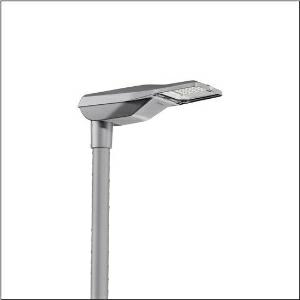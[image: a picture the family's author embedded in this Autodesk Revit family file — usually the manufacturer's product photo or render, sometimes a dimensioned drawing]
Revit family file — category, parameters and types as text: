
# Revit family: streetlight_sl_21_iq_micro___st1_5a_5xe1p31d08db_ec34
name_source: partatom
category: Lighting Fixtures
units: mm (PartAtom-declared; Revit-internal decimal feet)

## family parameters
Cut with Voids When Loaded = No
Host = Face
Light Source = No
Part Type = Normal
Room Calculation Point = No
Round Connector Dimension = Use Diameter
Shared = No

## types (1)
- --- (1 x LED, 4730 lm, 36.4 W, 3000K)
    Apparent Load = 36 VA
    CIE Flux Codes = 22 53 95 100 100
    Color Rendering = 70
    Color Temperature = 3000K
    Default Elevation = 1800 mm
    Description = Streetlight SL 21 iQ micro, mast luminaire, primary light control with lens, of PMMA, primary optical cover: cover, of toughened safety glass, transparent, light distribution: ST1.5a, light emission: direct distribution, primary light characteristic: asymmetric, installation type: post-top, side-entry, LED, High Power LED, rated luminous flux: 4.730lm, luminous efficacy: 130lm/W, light colour: 730, colour temperature: 3000K, control gear: iQ-Comfort, control: Auto-Match, Temp-Guard, Lumen-Switch, Night-Set, Smart-Wire, Light-Fading, Desk-Remote (wireless, voltage-free reading and setting of iQ features in the workshop via application-optimized NFC function/RFID function), optimised constant luminous flux control (CLO 2.0), pre-setting: linear dimming characteristic, mains connection: 220..240V, AC, 50/60Hz, start of lifetime: 36W, end of service life: 38W, reduction: 16W, luminaire housing, of diecast aluminium, powder-coated, Siteco® metallic grey (DB 702S), corrosivity category C5 mid according to DIN EN ISO 12944, please order mast flange separately, inclination adjustable: 0°, 5°, 10°, 15°, sealing non-destructively replaceable, multi-level sealing system, length: 528mm, width: 235mm, height: 110mm, mast flange for spigot size: 42mm (side-entry): 5XC10008XM4, 60/48mm (side-entry/post-top): 5XC10108XM2, 76/60mm (side-entry/post-top): 5XC10108XM1, protection rating (complete): IP66, insulation class (complete): insulation class II (safety insulation), certification: CE, ENEC, ENEC+, VDE, impact resistance: IK10, permissible operating ambient temperature for outdoor applications: -40..+50°C, standard-compliant lighting for roads and squares, packaging unit: 1 piece

Light Distribution: ST1.5a
    Height = 110 mm
    Lamp = 1 x LED
    Lamp Light Flux = 4730 lm
    Lamp Power = 36.4 W
    Lamp count = 1
    Length = 528 mm
    Luminous efficacy = 130 lm/W
    Manufacturer = Siteco
    ModVariant = No
    Model = 5XE1P31D08DB
    Number of Poles = 1
    OnlyDefault = Yes
    Power Factor = 1
    Product Name = Streetlight SL 21 iQ micro | ST1.5a
    Product group = mast luminaire | pylon top
    ProductGroupID = 6100
    Protection Class = Protection class II
    Protection Degree = IP 66
    RLX_Detail_Level = 1
    RLX_Emergency_Light_Flux = 0 lm
    RLX_Emergency_Type = 0
    RLX_Emergency_Type_DB = No
    RlxData = <blob elided: 103449 chars, md5=a06d8aaa>
    Socket = socket
    Standby Power = 0 W
    System Light Flux = 4730 lm
    System Power = 36 W
    Type Comments = factory setting: luminous flux: 100 % | dim-lin: 254 | 715 mA
    Type Image = l_1006881.jpg
    URL = http://relux.com
    VarID = @adj_153940
    Voltage = 0 V
    Weight = 0.00 kg
    Width = 235 mm

## geometry (parser evidence)
native form markers: Blend x4, Sweep x9
no freeform markers — native parametric forms only
